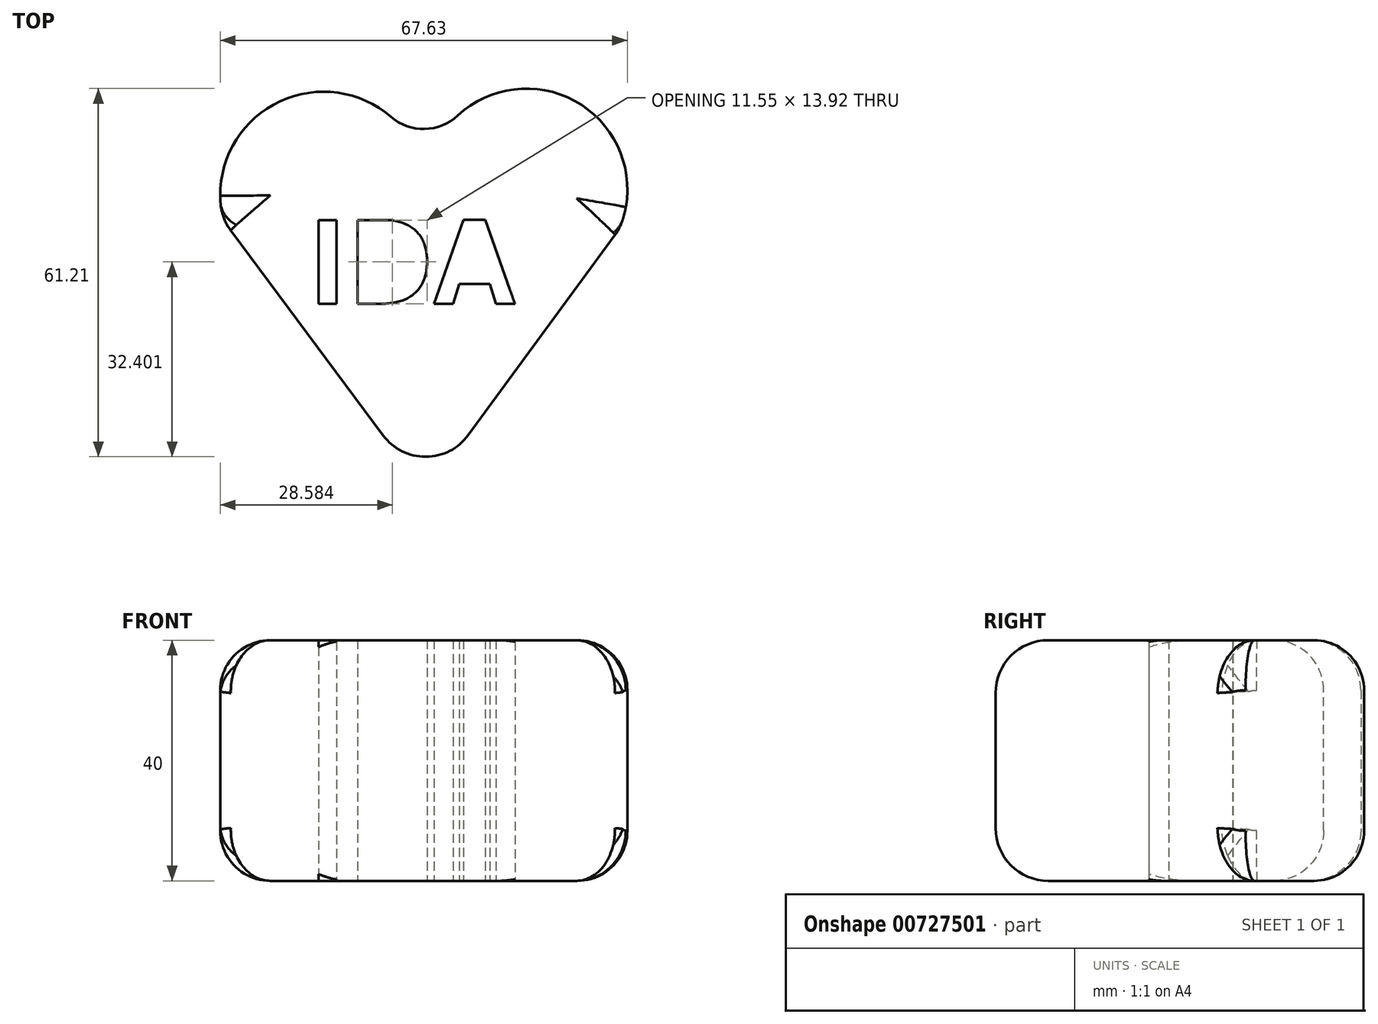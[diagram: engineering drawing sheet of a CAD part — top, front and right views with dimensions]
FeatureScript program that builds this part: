
annotation { "Feature Type Name" : "Feature", "Feature Type Description" : "" }
export const myFeature = defineFeature(function(context is Context, id is Id, definition is map)
    precondition{}
    {
        {
            var Q0;
            Q0=qCreatedBy(makeId("Top.planeOp"),FACE);
            var sketch = newSketch(context, id + "F0", { "sketchPlane" : qUnion([Q0])});
            skLineSegment(sketch, "E0", {"start": v(-33.62, 10.32) * mm, "end": v(0, -34.88) * mm});
            skLineSegment(sketch, "E1", {"start": v(0, -34.88) * mm, "end": v(32.08, 8.91) * mm});
            skArc(sketch, "E2", {"start": v(0, 16.77) * mm, "mid": v(-20.26, 31.5) * mm, "end": v(-33.62, 10.32) * mm});
            skArc(sketch, "E3", {"start": v(32.08, 8.91) * mm, "mid": v(20.7, 31.85) * mm, "end": v(0, 16.77) * mm});
            skText(sketch, "E4", { "text": "IDA", "fontName": "OpenSans-Bold.ttf"});
            skPoint(sketch, "E4.secondSnap0", {"position": v(16.04, -12.98) * mm});
            const initialGuessF0  = {"E4": [-0.01957, -0.00344, 1, 0, 0.01404]};
            skSetInitialGuess(sketch, initialGuessF0);
            skSolve(sketch);
        }
        {
            var Q0;
            Q0=makeQuery(id+"F0.imprint","IMPRINT",FACE,{"disambiguationData":[TD([[makeQuery(id+"F0.imprint","IMPRINT",EDGE,{"derivedFrom":sQuery(id+"F0.wireOp",EDGE,"E0")}),1.0]])]});
            extrude(context, id + "F1", {"entities" : qUnion([Q0]), "depth" : 40 * mm, "offsetDistance" : 25 * mm});
        }
        {
            var Q0;
            Q0=makeQuery(id+"F1.opExtrude","SWEPT_FACE",FACE,{"disambiguationData":[OSD([sQuery(id+"F0.wireOp",EDGE,"E0")])]});
            var Q1;
            Q1=makeQuery(id+"F1.opExtrude","SWEPT_FACE",FACE,{"disambiguationData":[OSD([sQuery(id+"F0.wireOp",EDGE,"E1")])]});
            fillet(context, id + "F2", {"entities" : qUnion([Q0, Q1]), "radius" : 8.77 * mm, "tangentPropagation" : true, "allowEdgeOverflow" : false});
        }
        {
            var Q0;
            Q0=makeQuery(id+"F1.opExtrude","SWEPT_FACE",FACE,{"disambiguationData":[OSD([sQuery(id+"F0.wireOp",EDGE,"E2")])]});
            var Q1;
            Q1=makeQuery(id+"F1.opExtrude","SWEPT_FACE",FACE,{"disambiguationData":[OSD([sQuery(id+"F0.wireOp",EDGE,"E3")])]});
            fillet(context, id + "F3", {"entities" : qUnion([Q0, Q1]), "radius" : 8.33 * mm, "tangentPropagation" : true, "allowEdgeOverflow" : false});
        }
    });
